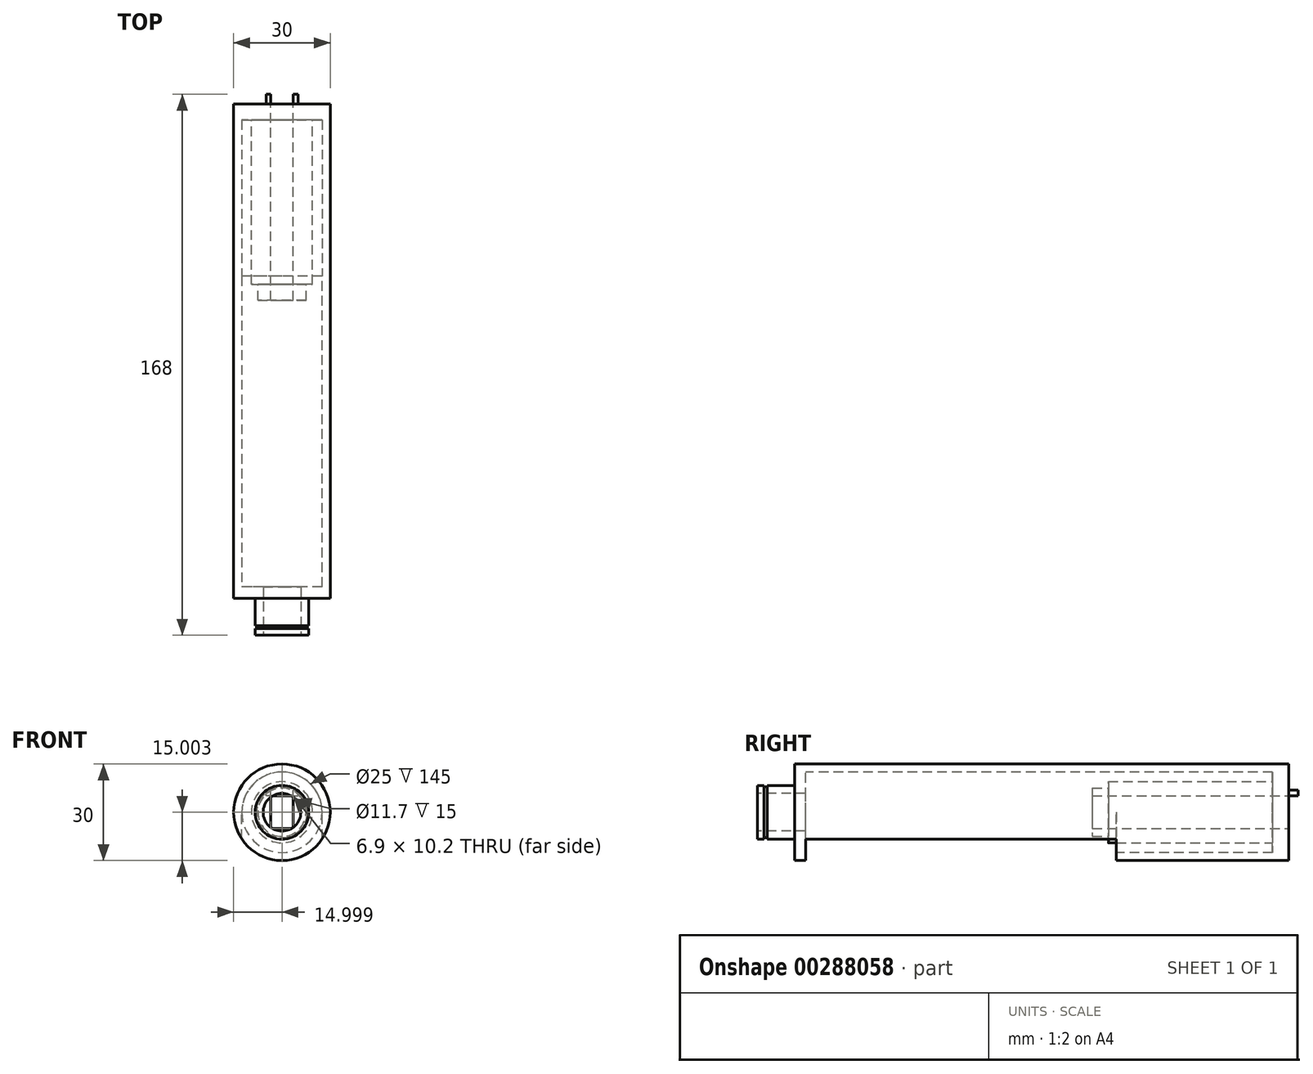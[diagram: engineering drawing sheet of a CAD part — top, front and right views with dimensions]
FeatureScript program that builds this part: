
annotation { "Feature Type Name" : "Feature", "Feature Type Description" : "" }
export const myFeature = defineFeature(function(context is Context, id is Id, definition is map)
    precondition{}
    {
        {
            var Q0;
            Q0=qCreatedBy(makeId("Front.planeOp"),FACE);
            var sketch = newSketch(context, id + "F0", { "sketchPlane" : qUnion([Q0])});
            skCircle(sketch, "E0", {"center": v(-30.66, 20.11) * mm, "radius": 12.5 * mm});
            skCircle(sketch, "E1", {"center": v(-30.66, 20.11) * mm, "radius": 15 * mm});
            skCircle(sketch, "E2", {"center": v(-30.66, 20.11) * mm, "radius": 5.85 * mm});
            skCircle(sketch, "E3", {"center": v(-30.66, 20.11) * mm, "radius": 8.35 * mm});
            skSolve(sketch);
        }
        {
            var Q0;
            Q0=makeQuery(id+"F0.imprint","IMPRINT",FACE,{"disambiguationData":[TD([[makeQuery(id+"F0.imprint","IMPRINT",EDGE,{"derivedFrom":sQuery(id+"F0.wireOp",EDGE,"E2")}),-1.0]])]});
            extrude(context, id + "F1", {"entities" : qUnion([Q0]), "oppositeDirection" : true, "depth" : 15 * mm});
        }
        {
            var Q0;
            Q0=makeQuery(id+"F0.imprint","IMPRINT",FACE,{"disambiguationData":[TD([[makeQuery(id+"F0.imprint","IMPRINT",EDGE,{"derivedFrom":sQuery(id+"F0.wireOp",EDGE,"E0")}),1.0]])]});
            var Q1;
            Q1=makeQuery(id+"F0.imprint","IMPRINT",FACE,{"disambiguationData":[TD([[makeQuery(id+"F0.imprint","IMPRINT",EDGE,{"derivedFrom":sQuery(id+"F0.wireOp",EDGE,"E0")}),-1.0]])]});
            extrude(context, id + "F2", {"entities" : qUnion([Q0, Q1]), "operationType" : NewBodyOperationType.ADD, "oppositeDirection" : true, "depth" : 15 * mm, "hasSecondDirection" : true, "secondDirectionOppositeDirection" : true, "secondDirectionDepth" : (15 - 3.5) * mm});
        }
        {
            var Q0;
            Q0=makeQuery(id+"F0.imprint","IMPRINT",FACE,{"disambiguationData":[TD([[makeQuery(id+"F0.imprint","IMPRINT",EDGE,{"derivedFrom":sQuery(id+"F0.wireOp",EDGE,"E0")}),-1.0]])]});
            extrude(context, id + "F3", {"entities" : qUnion([Q0]), "operationType" : NewBodyOperationType.ADD, "oppositeDirection" : true, "depth" : (150 + 15) * mm, "hasSecondDirection" : true, "secondDirectionOppositeDirection" : true, "secondDirectionDepth" : 15 * mm});
        }
        {
            var Q0;
            Q0=makeQuery(id+"F3.opExtrude","CAP_FACE",FACE,{"disambiguationData":[OSD([sQuery(id+"F0.wireOp",EDGE,"E0"),sQuery(id+"F0.wireOp",EDGE,"E1")])],"isStart":false});
            var sketch = newSketch(context, id + "F4", { "sketchPlane" : qUnion([Q0])});
            skCircle(sketch, "E4.0", {"center": v(30.66, 20.11) * mm, "radius": 15 * mm});
            skSolve(sketch);
        }
        {
            var Q0;
            Q0=makeQuery(id+"F4.imprint","IMPRINT",FACE,{"disambiguationData":[TD([[makeQuery(id+"F4.imprint","IMPRINT",EDGE,{"derivedFrom":makeQuery(id+"F3.opExtrude","CAP_EDGE",EDGE,{"disambiguationData":[OSD([sQuery(id+"F0.wireOp",EDGE,"E0")])],"isStart":false})}),-1.0]])]});
            var Q1;
            Q1=makeQuery(id+"F4.imprint","IMPRINT",FACE,{"disambiguationData":[TD([[makeQuery(id+"F4.imprint","IMPRINT",EDGE,{"derivedFrom":sQuery(id+"F4.wireOp",EDGE,"E4.0")}),-1.0]])]});
            extrude(context, id + "F5", {"entities" : qUnion([Q0, Q1]), "operationType" : NewBodyOperationType.ADD, "oppositeDirection" : true, "depth" : 5 * mm});
        }
        {
            var Q0;
            Q0=makeQuery(id+"F5.boolean.opBoolean","MERGE",FACE,{"derivedFrom":[makeQuery(id+"F3.opExtrude","CAP_FACE",FACE,{"disambiguationData":[OSD([sQuery(id+"F0.wireOp",EDGE,"E0"),sQuery(id+"F0.wireOp",EDGE,"E1")])],"isStart":false}),makeQuery(id+"F5.opExtrude","CAP_FACE",FACE,{"disambiguationData":[OSD([sQuery(id+"F4.wireOp",EDGE,"E4.0")])],"isStart":true})]});
            var sketch = newSketch(context, id + "F6", { "sketchPlane" : qUnion([Q0])});
            skCircle(sketch, "E5", {"center": v(30.66, 20.11) * mm, "radius": 9.5 * mm});
            skCircle(sketch, "E6", {"center": v(30.66, 20.11) * mm, "radius": 7.5 * mm});
            skLineSegment(sketch, "E7", {"start": v(30.66, 20.11) * mm, "end": v(30.66, 24.71) * mm});
            skLineSegment(sketch, "E8", {"start": v(30.66, 24.71) * mm, "end": v(33.61, 24.71) * mm});
            skLineSegment(sketch, "E9", {"start": v(14.49, 20.11) * mm, "end": v(47.26, 20.11) * mm, "construction": true});
            skLineSegment(sketch, "E10", {"start": v(30.66, 26.74) * mm, "end": v(30.66, 13.9) * mm, "construction": true});
            skLineSegment(sketch, "E11", {"start": v(33.61, 24.71) * mm, "end": v(33.61, 20.11) * mm});
            skLineSegment(sketch, "E12.MirrorCS", {"start": v(30.66, 15.51) * mm, "end": v(33.61, 15.51) * mm});
            skLineSegment(sketch, "E13.MirrorCS", {"start": v(33.61, 15.51) * mm, "end": v(33.61, 20.11) * mm});
            skLineSegment(sketch, "E14.MirrorCS", {"start": v(30.66, 15.51) * mm, "end": v(27.71, 15.51) * mm});
            skLineSegment(sketch, "E15.MirrorCS", {"start": v(27.71, 15.51) * mm, "end": v(27.71, 20.11) * mm});
            skLineSegment(sketch, "E16.MirrorCS", {"start": v(30.66, 24.71) * mm, "end": v(27.71, 24.71) * mm});
            skLineSegment(sketch, "E17.MirrorCS", {"start": v(27.71, 24.71) * mm, "end": v(27.71, 20.11) * mm});
            skLineSegment(sketch, "E18.0", {"start": v(30.66, 25.21) * mm, "end": v(34.11, 25.21) * mm});
            skLineSegment(sketch, "E18.1", {"start": v(34.11, 25.21) * mm, "end": v(34.11, 20.11) * mm});
            skLineSegment(sketch, "E18.2", {"start": v(30.66, 25.21) * mm, "end": v(27.21, 25.21) * mm});
            skLineSegment(sketch, "E18.3", {"start": v(34.11, 15.01) * mm, "end": v(34.11, 20.11) * mm});
            skLineSegment(sketch, "E18.4", {"start": v(27.21, 25.21) * mm, "end": v(27.21, 20.11) * mm});
            skLineSegment(sketch, "E18.5", {"start": v(27.21, 15.01) * mm, "end": v(27.21, 20.11) * mm});
            skLineSegment(sketch, "E18.6", {"start": v(30.66, 15.01) * mm, "end": v(27.21, 15.01) * mm});
            skLineSegment(sketch, "E18.7", {"start": v(30.66, 15.01) * mm, "end": v(34.11, 15.01) * mm});
            skLineSegment(sketch, "E19", {"start": v(9.3, 20.11) * mm, "end": v(53.08, 20.11) * mm});
            skLineSegment(sketch, "E20.bottom", {"start": v(27.21, 25.21) * mm, "end": v(25.7, 25.21) * mm});
            skLineSegment(sketch, "E20.top", {"start": v(27.21, 26.94) * mm, "end": v(25.7, 26.94) * mm});
            skLineSegment(sketch, "E20.left", {"start": v(27.21, 25.21) * mm, "end": v(27.21, 26.94) * mm});
            skLineSegment(sketch, "E20.right", {"start": v(25.7, 25.21) * mm, "end": v(25.7, 26.94) * mm});
            skLineSegment(sketch, "E21.MirrorCS", {"start": v(34.11, 26.94) * mm, "end": v(35.62, 26.94) * mm});
            skLineSegment(sketch, "E22.MirrorCS", {"start": v(35.62, 25.21) * mm, "end": v(35.62, 26.94) * mm});
            skLineSegment(sketch, "E23.MirrorCS", {"start": v(34.11, 25.21) * mm, "end": v(35.62, 25.21) * mm});
            skLineSegment(sketch, "E24.MirrorCS", {"start": v(34.11, 25.21) * mm, "end": v(34.11, 26.94) * mm});
            skSolve(sketch);
        }
        {
            var Q0;
            Q0=makeQuery(id+"F6.imprint","IMPRINT",FACE,{"disambiguationData":[TD([[makeQuery(id+"F6.imprint","IMPRINT",EDGE,{"derivedFrom":sQuery(id+"F6.wireOp",EDGE,"E5")}),1.0]])]});
            var Q1;
            {var subQ2=sQuery(id+"F6.wireOp",EDGE,"E20.top");Q1=makeQuery(id+"F6.imprint","IMPRINT",FACE,{"disambiguationData":[TD([[makeQuery(id+"F6.imprint","IMPRINT",EDGE,{"derivedFrom":subQ2}),-1.0]])]});}
            var Q2;
            {var subQ5=sQuery(id+"F6.wireOp",EDGE,"E20.top");Q2=makeQuery(id+"F6.imprint","IMPRINT",FACE,{"disambiguationData":[TD([[makeQuery(id+"F6.imprint","IMPRINT",EDGE,{"derivedFrom":subQ5}),1.0]])]});}
            var Q3;
            {var subQ5=sQuery(id+"F6.wireOp",EDGE,"E21.MirrorCS");Q3=makeQuery(id+"F6.imprint","IMPRINT",FACE,{"disambiguationData":[TD([[makeQuery(id+"F6.imprint","IMPRINT",EDGE,{"derivedFrom":subQ5}),-1.0]])]});}
            extrude(context, id + "F7", {"entities" : qUnion([Q0, Q1, Q2, Q3]), "operationType" : NewBodyOperationType.ADD, "oppositeDirection" : true, "depth" : (56) * mm, "hasSecondDirection" : true, "secondDirectionOppositeDirection" : true, "secondDirectionDepth" : 5 * mm});
        }
        {
            var Q0;
            Q0=makeQuery(id+"F6.imprint","IMPRINT",FACE,{"disambiguationData":[TD([[makeQuery(id+"F6.imprint","IMPRINT",EDGE,{"derivedFrom":sQuery(id+"F6.wireOp",EDGE,"E6")}),1.0]])]});
            var Q1;
            {var subQ6=sQuery(id+"F6.wireOp",EDGE,"E18.0");Q1=makeQuery(id+"F6.imprint","IMPRINT",FACE,{"disambiguationData":[TD([[makeQuery(id+"F6.imprint","IMPRINT",EDGE,{"derivedFrom":subQ6}),1.0]])]});}
            var Q2;
            {var subQ0=sQuery(id+"F6.wireOp",EDGE,"E18.1");Q2=makeQuery(id+"F6.imprint","IMPRINT",FACE,{"disambiguationData":[TD([[makeQuery(id+"F6.imprint","IMPRINT",EDGE,{"derivedFrom":subQ0}),1.0]])]});}
            var Q3;
            {var subQ2=sQuery(id+"F6.wireOp",EDGE,"E18.4");Q3=makeQuery(id+"F6.imprint","IMPRINT",FACE,{"disambiguationData":[TD([[makeQuery(id+"F6.imprint","IMPRINT",EDGE,{"derivedFrom":subQ2}),-1.0]])]});}
            var Q4;
            {var subQ0=sQuery(id+"F6.wireOp",EDGE,"E18.3");Q4=makeQuery(id+"F6.imprint","IMPRINT",FACE,{"disambiguationData":[TD([[makeQuery(id+"F6.imprint","IMPRINT",EDGE,{"derivedFrom":subQ0}),-1.0]])]});}
            extrude(context, id + "F8", {"entities" : qUnion([Q0, Q1, Q2, Q3, Q4]), "operationType" : NewBodyOperationType.ADD, "oppositeDirection" : true, "depth" : (56 + 5) * mm});
        }
        {
            var Q0;
            Q0=makeQuery(id+"F6.imprint","IMPRINT",FACE,{"disambiguationData":[TD([[makeQuery(id+"F6.imprint","IMPRINT",EDGE,{"derivedFrom":sQuery(id+"F6.wireOp",EDGE,"E8")}),-1.0]])]});
            var Q1;
            Q1=makeQuery(id+"F6.imprint","IMPRINT",FACE,{"disambiguationData":[TD([[makeQuery(id+"F6.imprint","IMPRINT",EDGE,{"derivedFrom":sQuery(id+"F6.wireOp",EDGE,"E8")}),1.0]])]});
            var Q2;
            Q2=makeQuery(id+"F6.imprint","IMPRINT",FACE,{"disambiguationData":[TD([[makeQuery(id+"F6.imprint","IMPRINT",EDGE,{"derivedFrom":sQuery(id+"F6.wireOp",EDGE,"E12.MirrorCS")}),1.0]])]});
            var Q3;
            {var subQ0=sQuery(id+"F6.wireOp",EDGE,"E7");Q3=makeQuery(id+"F6.imprint","IMPRINT",FACE,{"disambiguationData":[TD([[makeQuery(id+"F6.imprint","IMPRINT",EDGE,{"derivedFrom":subQ0}),1.0]])]});}
            var Q4;
            Q4=makeQuery(id+"F6.imprint","IMPRINT",FACE,{"disambiguationData":[TD([[makeQuery(id+"F6.imprint","IMPRINT",EDGE,{"derivedFrom":sQuery(id+"F6.wireOp",EDGE,"E12.MirrorCS")}),-1.0]])]});
            extrude(context, id + "F9", {"entities" : qUnion([Q0, Q1, Q2, Q3, Q4]), "operationType" : NewBodyOperationType.REMOVE, "oppositeDirection" : true, "depth" : 15.5 * mm});
        }
        {
            var Q0;
            Q0=sQuery(id+"F6.wireOp",EDGE,"E19");
            extrude(context, id + "F10", {"bodyType" : ToolBodyType.SURFACE, "surfaceEntities" : qUnion([Q0]), "oppositeDirection" : true, "depth" : 178 * mm});
        }
        {
            var Q0;
            Q0=makeQuery(id+"F10.opExtrude","SWEPT_FACE",FACE,{"disambiguationData":[OSD([sQuery(id+"F6.wireOp",EDGE,"E19")])]});
            var sketch = newSketch(context, id + "F11", { "sketchPlane" : qUnion([Q0])});
            skLineSegment(sketch, "E25.0", {"start": v(-18.16, 15) * mm, "end": v(-43.16, 15) * mm});
            skLineSegment(sketch, "E26", {"start": v(-18.16, 15) * mm, "end": v(-18.16, 111.5) * mm});
            skLineSegment(sketch, "E27", {"start": v(-18.16, 111.5) * mm, "end": v(-43.16, 111.5) * mm});
            skLineSegment(sketch, "E28", {"start": v(-43.16, 111.5) * mm, "end": v(-43.16, 15) * mm});
            skLineSegment(sketch, "E29", {"start": v(-21.16, 93.43) * mm, "end": v(-21.16, 111.5) * mm});
            skLineSegment(sketch, "E30", {"start": v(-40.16, 93.43) * mm, "end": v(-40.16, 111.5) * mm});
            skLineSegment(sketch, "E31", {"start": v(-21.16, 93.43) * mm, "end": v(-40.16, 93.43) * mm});
            skSolve(sketch);
        }
        {
            var Q0;
            Q0=makeQuery(id+"F11.imprint","IMPRINT",FACE,{"disambiguationData":[TD([[makeQuery(id+"F11.imprint","IMPRINT",EDGE,{"derivedFrom":sQuery(id+"F11.wireOp",EDGE,"E25.0")}),-1.0]])]});
            extrude(context, id + "F12", {"entities" : qUnion([Q0]), "operationType" : NewBodyOperationType.REMOVE, "oppositeDirection" : true, "depth" : 25 * mm});
        }
        {
            var Q0;
            Q0=makeQuery(id+"F12.boolean.opBoolean","COPY",FACE,{"derivedFrom":makeQuery(id+"F12.opExtrude","SWEPT_FACE",FACE,{"disambiguationData":[OSD([sQuery(id+"F11.wireOp",EDGE,"E31")])]})});
            var sketch = newSketch(context, id + "F13", { "sketchPlane" : qUnion([Q0])});
            skArc(sketch, "E32.0", {"start": v(-40.16, 8.5) * mm, "mid": v(-30.66, 5.11) * mm, "end": v(-21.16, 8.5) * mm});
            skArc(sketch, "E32.1", {"start": v(-40.16, 11.99) * mm, "mid": v(-30.66, 7.61) * mm, "end": v(-21.16, 11.99) * mm});
            skLineSegment(sketch, "E33.0", {"start": v(-40.16, 8.5) * mm, "end": v(-40.16, 11.99) * mm});
            skLineSegment(sketch, "E33.1", {"start": v(-21.16, 8.5) * mm, "end": v(-21.16, 11.99) * mm});
            skSolve(sketch);
        }
        {
            var Q0;
            Q0=makeQuery(id+"F13.imprint","IMPRINT",FACE,{"disambiguationData":[TD([[makeQuery(id+"F13.imprint","IMPRINT",EDGE,{"derivedFrom":sQuery(id+"F13.wireOp",EDGE,"E32.0")}),1.0]])]});
            var Q1;
            {var subQ0=sQuery(id+"F11.wireOp",EDGE,"E27");Q1=makeQuery(id+"F12.boolean.opBoolean","COPY",FACE,{"derivedFrom":makeQuery(id+"F12.opExtrude","SWEPT_FACE",FACE,{"disambiguationData":[OSD([subQ0]),TDD([makeQuery(id+"F11.imprint","IMPRINT",EDGE,{"disambiguationData":[TD([[makeQuery(id+"F11.imprint","INTERSECT",VERTEX,{"derivedFrom":[sQuery(id+"F11.wireOp",EDGE,"E26"),subQ0]}),-1.0]])],"derivedFrom":subQ0})])]})});}
            extrude(context, id + "F14", {"entities" : qUnion([Q0]), "operationType" : NewBodyOperationType.REMOVE, "endBound" : BoundingType.UP_TO_SURFACE, "oppositeDirection" : true, "endBoundEntityFace" : qUnion([Q1]), "depth" : 25 * mm});
        }
        {
            var Q0;
            {var subQ5=sQuery(id+"F6.wireOp",EDGE,"E20.bottom");Q0=makeQuery(id+"F6.imprint","IMPRINT",FACE,{"disambiguationData":[TD([[makeQuery(id+"F6.imprint","IMPRINT",EDGE,{"derivedFrom":subQ5}),-1.0]])]});}
            var Q1;
            {var subQ5=sQuery(id+"F6.wireOp",EDGE,"E20.top");Q1=makeQuery(id+"F6.imprint","IMPRINT",FACE,{"disambiguationData":[TD([[makeQuery(id+"F6.imprint","IMPRINT",EDGE,{"derivedFrom":subQ5}),1.0]])]});}
            var Q2;
            {var subQ5=sQuery(id+"F6.wireOp",EDGE,"E23.MirrorCS");Q2=makeQuery(id+"F6.imprint","IMPRINT",FACE,{"disambiguationData":[TD([[makeQuery(id+"F6.imprint","IMPRINT",EDGE,{"derivedFrom":subQ5}),1.0]])]});}
            var Q3;
            {var subQ5=sQuery(id+"F6.wireOp",EDGE,"E21.MirrorCS");Q3=makeQuery(id+"F6.imprint","IMPRINT",FACE,{"disambiguationData":[TD([[makeQuery(id+"F6.imprint","IMPRINT",EDGE,{"derivedFrom":subQ5}),-1.0]])]});}
            extrude(context, id + "F15", {"entities" : qUnion([Q0, Q1, Q2, Q3]), "operationType" : NewBodyOperationType.ADD, "depth" : 3 * mm});
        }
        {
            var Q0;
            Q0=makeQuery(id+"F1.opExtrude","CAP_FACE",FACE,{"disambiguationData":[OSD([sQuery(id+"F0.wireOp",EDGE,"E2"),sQuery(id+"F0.wireOp",EDGE,"E3")])],"isStart":true});
            var sketch = newSketch(context, id + "F16", { "sketchPlane" : qUnion([Q0])});
            skCircle(sketch, "E34.0", {"center": v(-30.66, 20.11) * mm, "radius": 8.35 * mm});
            skCircle(sketch, "E35", {"center": v(-30.66, 20.11) * mm, "radius": 7.85 * mm});
            skSolve(sketch);
        }
        {
            var Q0;
            Q0=makeQuery(id+"F16.imprint","IMPRINT",FACE,{"disambiguationData":[TD([[makeQuery(id+"F16.imprint","IMPRINT",EDGE,{"derivedFrom":sQuery(id+"F16.wireOp",EDGE,"E34.0")}),1.0]])]});
            extrude(context, id + "F17", {"entities" : qUnion([Q0]), "operationType" : NewBodyOperationType.REMOVE, "oppositeDirection" : true, "depth" : 3 * mm, "hasSecondDirection" : true, "secondDirectionOppositeDirection" : true, "secondDirectionDepth" : 2 * mm});
        }
    });
